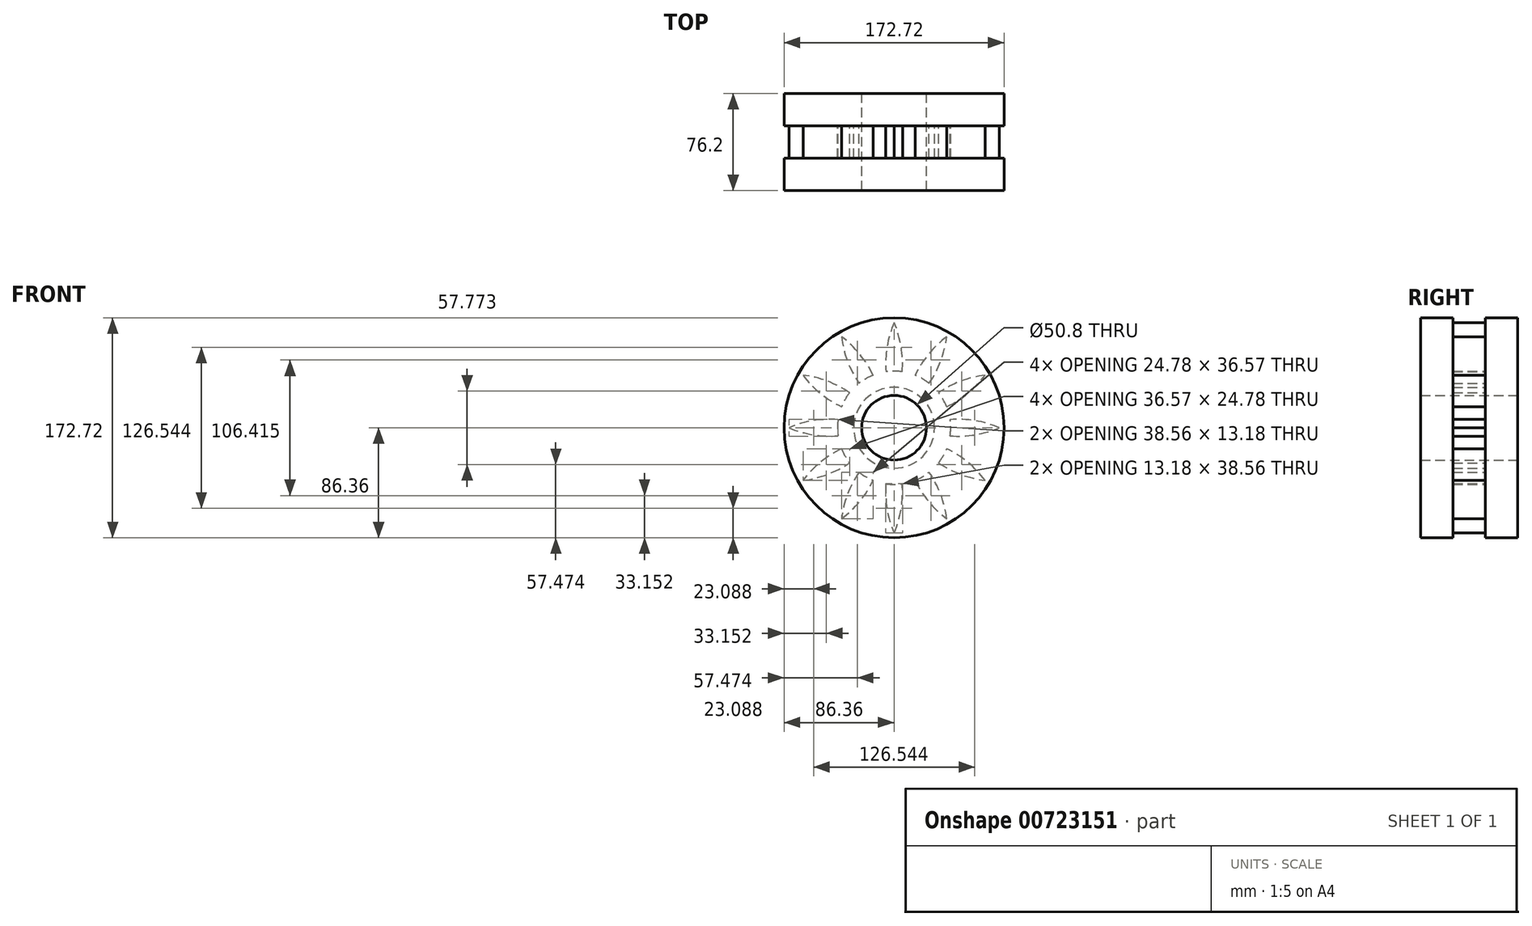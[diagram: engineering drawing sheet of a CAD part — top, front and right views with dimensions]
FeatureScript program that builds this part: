
annotation { "Feature Type Name" : "Feature", "Feature Type Description" : "" }
export const myFeature = defineFeature(function(context is Context, id is Id, definition is map)
    precondition{}
    {
        {
            var Q0;
            Q0=qCreatedBy(makeId("Front.planeOp"),FACE);
            var sketch = newSketch(context, id + "F0", { "sketchPlane" : qUnion([Q0])});
            skCircle(sketch, "E0", {"center": v(0, 0) * mm, "radius": 25.4 * mm});
            skCircle(sketch, "E1.0", {"center": v(0, 0) * mm, "radius": 31.75 * mm});
            skPoint(sketch, "E2.start.orphan", {"position": v(0, 76) * mm});
            skCircle(sketch, "E3.0", {"center": v(0, 0) * mm, "radius": 44.45 * mm});
            skArc(sketch, "E4", {"start": v(82.55, 0) * mm, "mid": v(63.66, 5.52) * mm, "end": v(44, 6.35) * mm});
            skArc(sketch, "E5", {"start": v(44, -6.35) * mm, "mid": v(63.66, -5.52) * mm, "end": v(82.55, 0) * mm});
            skArc(sketch, "E6.1.0", {"start": v(71.5, 41.27) * mm, "mid": v(52.37, 36.6) * mm, "end": v(34.92, 27.5) * mm});
            skArc(sketch, "E6.1.1", {"start": v(41.27, 16.5) * mm, "mid": v(57.89, 27.05) * mm, "end": v(71.5, 41.27) * mm});
            skArc(sketch, "E6.2.0", {"start": v(41.27, 71.5) * mm, "mid": v(27.05, 57.89) * mm, "end": v(16.5, 41.27) * mm});
            skArc(sketch, "E6.2.1", {"start": v(27.5, 34.92) * mm, "mid": v(36.6, 52.37) * mm, "end": v(41.27, 71.5) * mm});
            skArc(sketch, "E6.3.0", {"start": v(0, 82.55) * mm, "mid": v(-5.52, 63.66) * mm, "end": v(-6.35, 44) * mm});
            skArc(sketch, "E6.3.1", {"start": v(6.35, 44) * mm, "mid": v(5.52, 63.66) * mm, "end": v(0, 82.55) * mm});
            skArc(sketch, "E6.4.0", {"start": v(-41.27, 71.5) * mm, "mid": v(-36.6, 52.37) * mm, "end": v(-27.5, 34.92) * mm});
            skArc(sketch, "E6.4.1", {"start": v(-16.5, 41.27) * mm, "mid": v(-27.05, 57.89) * mm, "end": v(-41.27, 71.5) * mm});
            skArc(sketch, "E6.5.0", {"start": v(-71.5, 41.27) * mm, "mid": v(-57.89, 27.05) * mm, "end": v(-41.27, 16.5) * mm});
            skArc(sketch, "E6.5.1", {"start": v(-34.92, 27.5) * mm, "mid": v(-52.37, 36.6) * mm, "end": v(-71.5, 41.27) * mm});
            skArc(sketch, "E6.6.0", {"start": v(-82.55, 0) * mm, "mid": v(-63.66, -5.52) * mm, "end": v(-44, -6.35) * mm});
            skArc(sketch, "E6.6.1", {"start": v(-44, 6.35) * mm, "mid": v(-63.66, 5.52) * mm, "end": v(-82.55, 0) * mm});
            skArc(sketch, "E6.7.0", {"start": v(-71.5, -41.27) * mm, "mid": v(-52.37, -36.6) * mm, "end": v(-34.92, -27.5) * mm});
            skArc(sketch, "E6.7.1", {"start": v(-41.27, -16.5) * mm, "mid": v(-57.89, -27.05) * mm, "end": v(-71.5, -41.27) * mm});
            skArc(sketch, "E6.8.0", {"start": v(-41.27, -71.5) * mm, "mid": v(-27.05, -57.89) * mm, "end": v(-16.5, -41.27) * mm});
            skArc(sketch, "E6.8.1", {"start": v(-27.5, -34.92) * mm, "mid": v(-36.6, -52.37) * mm, "end": v(-41.27, -71.5) * mm});
            skArc(sketch, "E6.9.0", {"start": v(0, -82.55) * mm, "mid": v(5.52, -63.66) * mm, "end": v(6.35, -44) * mm});
            skArc(sketch, "E6.9.1", {"start": v(-6.35, -44) * mm, "mid": v(-5.52, -63.66) * mm, "end": v(0, -82.55) * mm});
            skArc(sketch, "E6.10.0", {"start": v(41.27, -71.5) * mm, "mid": v(36.6, -52.37) * mm, "end": v(27.5, -34.92) * mm});
            skArc(sketch, "E6.10.1", {"start": v(16.5, -41.27) * mm, "mid": v(27.05, -57.89) * mm, "end": v(41.27, -71.5) * mm});
            skArc(sketch, "E6.11.0", {"start": v(71.5, -41.27) * mm, "mid": v(57.89, -27.05) * mm, "end": v(41.27, -16.5) * mm});
            skArc(sketch, "E6.11.1", {"start": v(34.92, -27.5) * mm, "mid": v(52.37, -36.6) * mm, "end": v(71.5, -41.27) * mm});
            skSolve(sketch);
        }
        {
            var Q0;
            {var subQ0=sQuery(id+"F0.wireOp",EDGE,"E6.3.0");Q0=makeQuery(id+"F0.imprint","IMPRINT",FACE,{"disambiguationData":[TD([[makeQuery(id+"F0.imprint","IMPRINT",EDGE,{"derivedFrom":subQ0}),1.0]])]});}
            var Q1;
            {var subQ0=sQuery(id+"F0.wireOp",EDGE,"E6.4.0");Q1=makeQuery(id+"F0.imprint","IMPRINT",FACE,{"disambiguationData":[TD([[makeQuery(id+"F0.imprint","IMPRINT",EDGE,{"derivedFrom":subQ0}),1.0]])]});}
            var Q2;
            {var subQ0=sQuery(id+"F0.wireOp",EDGE,"E6.5.0");Q2=makeQuery(id+"F0.imprint","IMPRINT",FACE,{"disambiguationData":[TD([[makeQuery(id+"F0.imprint","IMPRINT",EDGE,{"derivedFrom":subQ0}),1.0]])]});}
            var Q3;
            {var subQ0=sQuery(id+"F0.wireOp",EDGE,"E6.6.0");Q3=makeQuery(id+"F0.imprint","IMPRINT",FACE,{"disambiguationData":[TD([[makeQuery(id+"F0.imprint","IMPRINT",EDGE,{"derivedFrom":subQ0}),1.0]])]});}
            var Q4;
            {var subQ0=sQuery(id+"F0.wireOp",EDGE,"E6.7.0");Q4=makeQuery(id+"F0.imprint","IMPRINT",FACE,{"disambiguationData":[TD([[makeQuery(id+"F0.imprint","IMPRINT",EDGE,{"derivedFrom":subQ0}),1.0]])]});}
            var Q5;
            {var subQ0=sQuery(id+"F0.wireOp",EDGE,"E6.8.0");Q5=makeQuery(id+"F0.imprint","IMPRINT",FACE,{"disambiguationData":[TD([[makeQuery(id+"F0.imprint","IMPRINT",EDGE,{"derivedFrom":subQ0}),1.0]])]});}
            var Q6;
            {var subQ0=sQuery(id+"F0.wireOp",EDGE,"E6.9.0");Q6=makeQuery(id+"F0.imprint","IMPRINT",FACE,{"disambiguationData":[TD([[makeQuery(id+"F0.imprint","IMPRINT",EDGE,{"derivedFrom":subQ0}),1.0]])]});}
            var Q7;
            {var subQ0=sQuery(id+"F0.wireOp",EDGE,"E6.10.0");Q7=makeQuery(id+"F0.imprint","IMPRINT",FACE,{"disambiguationData":[TD([[makeQuery(id+"F0.imprint","IMPRINT",EDGE,{"derivedFrom":subQ0}),1.0]])]});}
            var Q8;
            {var subQ0=sQuery(id+"F0.wireOp",EDGE,"E6.11.0");Q8=makeQuery(id+"F0.imprint","IMPRINT",FACE,{"disambiguationData":[TD([[makeQuery(id+"F0.imprint","IMPRINT",EDGE,{"derivedFrom":subQ0}),1.0]])]});}
            var Q9;
            {var subQ0=sQuery(id+"F0.wireOp",EDGE,"E4");Q9=makeQuery(id+"F0.imprint","IMPRINT",FACE,{"disambiguationData":[TD([[makeQuery(id+"F0.imprint","IMPRINT",EDGE,{"derivedFrom":subQ0}),1.0]])]});}
            var Q10;
            {var subQ0=sQuery(id+"F0.wireOp",EDGE,"E6.1.0");Q10=makeQuery(id+"F0.imprint","IMPRINT",FACE,{"disambiguationData":[TD([[makeQuery(id+"F0.imprint","IMPRINT",EDGE,{"derivedFrom":subQ0}),1.0]])]});}
            var Q11;
            {var subQ0=sQuery(id+"F0.wireOp",EDGE,"E6.2.0");Q11=makeQuery(id+"F0.imprint","IMPRINT",FACE,{"disambiguationData":[TD([[makeQuery(id+"F0.imprint","IMPRINT",EDGE,{"derivedFrom":subQ0}),1.0]])]});}
            var Q12;
            Q12=makeQuery(id+"F0.imprint","IMPRINT",FACE,{"disambiguationData":[TD([[makeQuery(id+"F0.imprint","IMPRINT",EDGE,{"derivedFrom":sQuery(id+"F0.wireOp",EDGE,"E1.0")}),-1.0]])]});
            var Q13;
            Q13=makeQuery(id+"F0.imprint","IMPRINT",FACE,{"disambiguationData":[TD([[makeQuery(id+"F0.imprint","IMPRINT",EDGE,{"derivedFrom":sQuery(id+"F0.wireOp",EDGE,"E0")}),-1.0]])]});
            extrude(context, id + "F1", {"entities" : qUnion([Q0, Q1, Q2, Q3, Q4, Q5, Q6, Q7, Q8, Q9, Q10, Q11, Q12, Q13]), "depth" : 25.4 * mm, "offsetDistance" : 25.4 * mm});
        }
        {
            var Q0;
            Q0=qCreatedBy(makeId("Front.planeOp"),FACE);
            var sketch = newSketch(context, id + "F2", { "sketchPlane" : qUnion([Q0])});
            skCircle(sketch, "E7", {"center": v(0, 0) * mm, "radius": 86.36 * mm});
            skSolve(sketch);
        }
        {
            var Q0;
            Q0=makeQuery(id+"F2.imprint","IMPRINT",FACE,{"disambiguationData":[TD([[makeQuery(id+"F2.imprint","IMPRINT",EDGE,{"derivedFrom":sQuery(id+"F2.wireOp",EDGE,"E7")}),1.0]])]});
            extrude(context, id + "F3", {"entities" : qUnion([Q0]), "operationType" : NewBodyOperationType.ADD, "oppositeDirection" : true, "depth" : 25.4 * mm, "offsetDistance" : 25.4 * mm});
        }
        {
            var Q0;
            Q0=makeQuery(id+"F3.boolean.opBoolean","SPLIT",FACE,{"disambiguationData":[TD([makeQuery(id+"F1.opExtrude","SWEPT_FACE",FACE,{"disambiguationData":[OSD([sQuery(id+"F0.wireOp",EDGE,"E0")])]})])],"derivedFrom":makeQuery(id+"F3.opExtrude","CAP_FACE",FACE,{"disambiguationData":[OSD([sQuery(id+"F2.wireOp",EDGE,"E7")])],"isStart":true})});
            extrude(context, id + "F4", {"entities" : qUnion([Q0]), "operationType" : NewBodyOperationType.REMOVE, "oppositeDirection" : true, "depth" : 50.8 * mm, "offsetDistance" : 25.4 * mm});
        }
        {
            var Q0;
            Q0=makeQuery(id+"F1.opExtrude","CAP_FACE",FACE,{"disambiguationData":[OSD([sQuery(id+"F0.wireOp",EDGE,"E0"),sQuery(id+"F0.wireOp",EDGE,"E3.0"),sQuery(id+"F0.wireOp",EDGE,"E4"),sQuery(id+"F0.wireOp",EDGE,"E5"),sQuery(id+"F0.wireOp",EDGE,"E6.1.0"),sQuery(id+"F0.wireOp",EDGE,"E6.1.1"),sQuery(id+"F0.wireOp",EDGE,"E6.2.0"),sQuery(id+"F0.wireOp",EDGE,"E6.2.1"),sQuery(id+"F0.wireOp",EDGE,"E6.3.0"),sQuery(id+"F0.wireOp",EDGE,"E6.3.1"),sQuery(id+"F0.wireOp",EDGE,"E6.4.0"),sQuery(id+"F0.wireOp",EDGE,"E6.4.1"),sQuery(id+"F0.wireOp",EDGE,"E6.5.0"),sQuery(id+"F0.wireOp",EDGE,"E6.5.1"),sQuery(id+"F0.wireOp",EDGE,"E6.6.0"),sQuery(id+"F0.wireOp",EDGE,"E6.6.1"),sQuery(id+"F0.wireOp",EDGE,"E6.7.0"),sQuery(id+"F0.wireOp",EDGE,"E6.7.1"),sQuery(id+"F0.wireOp",EDGE,"E6.8.0"),sQuery(id+"F0.wireOp",EDGE,"E6.8.1"),sQuery(id+"F0.wireOp",EDGE,"E6.9.0"),sQuery(id+"F0.wireOp",EDGE,"E6.9.1"),sQuery(id+"F0.wireOp",EDGE,"E6.10.0"),sQuery(id+"F0.wireOp",EDGE,"E6.10.1"),sQuery(id+"F0.wireOp",EDGE,"E6.11.0"),sQuery(id+"F0.wireOp",EDGE,"E6.11.1")])],"isStart":false});
            var sketch = newSketch(context, id + "F5", { "sketchPlane" : qUnion([Q0])});
            skCircle(sketch, "E8", {"center": v(0, 0) * mm, "radius": 86.36 * mm});
            skCircle(sketch, "E9", {"center": v(0, 0) * mm, "radius": 25.4 * mm});
            skSolve(sketch);
        }
        {
            var Q0;
            Q0 = qSketchRegion(id + "F5", true);
            extrude(context, id + "F6", {"entities" : qUnion([Q0]), "operationType" : NewBodyOperationType.ADD, "depth" : 25.4 * mm, "offsetDistance" : 25.4 * mm});
        }
    });
